# Revit family: Rotor 3500 Series - 3504PC
name_source: partatom
category: Acessórios do tubo
units: mm (PartAtom-declared; Revit-internal decimal feet)

## family parameters
Com base no plano de trabalho = Não
Compartilhado = Não
Corte com vazios quando carregada = Não
Cota do conector redondo = Utilizar diâmetro
Número OmniClass = 23.60.30.11.14
Sempre na vertical = Sim
Tipo de parte = Normal
Título OmniClass = Pipework Fittings

## types (6) — shared parameters
Angle = 25.00°
Black Plastic = Black Plastic
Blue = Blue Plastic
Body height = 1 '
Descrição = 3504PC: 4 Rotor
Fabricante = Rain Bird
Modelo = 3504PC
RainBird: Code = Y34000
RainBird: Description = 3504PC: 4 Rotor
RainBird: Product Link = https://www.rainbird.com
Side inlet = Não
SupportProjetos: Level of Detail = LOD 300
SupportProjetos: Reviw = R00
TABLE 25 = TABLE 25psi
TABLE 35 = TABLE 35psi
TABLE 45 = TABLE 45psi
TABLE 55 = TABLE 55psi
TABLE PRESSURE = Press.
URL = https://www.rainbird.com
Water = Water
zero-valued in all types: Conection, DD1, DD10, DD11, DD12, DD13, DD3, DD4, DD5, DD7, Elevação padrão, H1, Pop up height, R1, R2, R3, R4, R5, RN, RT

## per-type parameters (varying)
| type | Instance |
| Nozzle 0.75 | 1 |
| Nozzle 1.0 | 2 |
| Nozzle 1.5 | 3 |
| Nozzle 2.0 | 4 |
| Nozzle 3.0 | 5 |
| Nozzle 4.0 | 6 |
